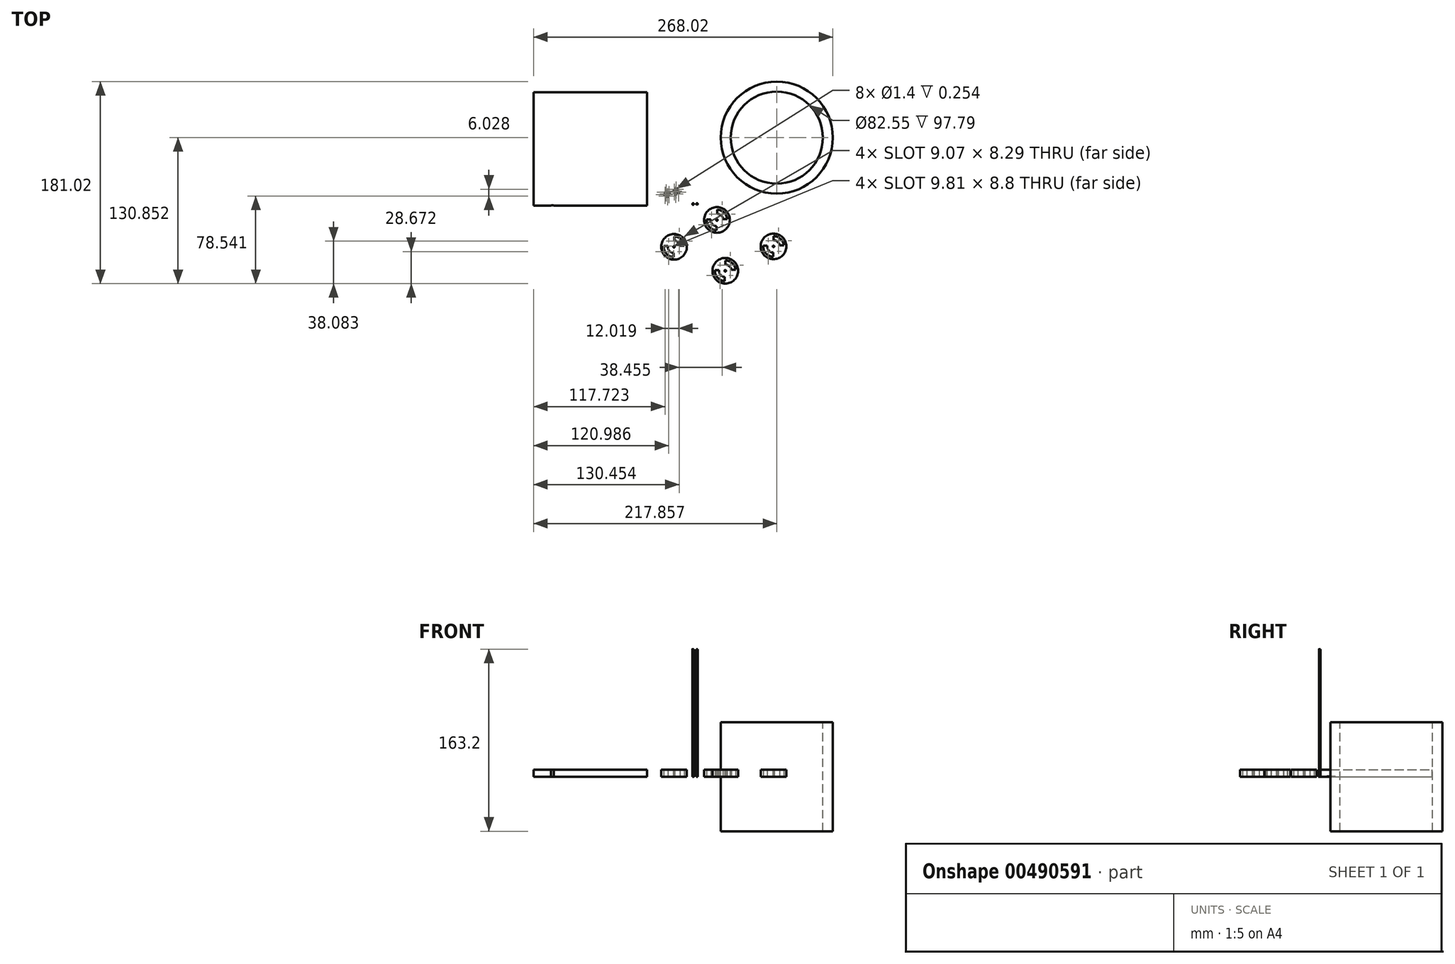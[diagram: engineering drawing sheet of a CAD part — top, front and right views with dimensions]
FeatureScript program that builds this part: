
annotation { "Feature Type Name" : "Feature", "Feature Type Description" : "" }
export const myFeature = defineFeature(function(context is Context, id is Id, definition is map)
    precondition{}
    {
        {
            var Q0;
            Q0=qCreatedBy(makeId("Top.planeOp"),FACE);
            var sketch = newSketch(context, id + "F0", { "sketchPlane" : qUnion([Q0])});
            skPoint(sketch, "E0.middle", {"position": v(-57.24, 51.22) * mm});
            skLineSegment(sketch, "E1.bottom", {"start": v(-104.05, -41.76) * mm, "end": v(-2.45, -41.76) * mm});
            skLineSegment(sketch, "E1.top", {"start": v(-104.05, 59.84) * mm, "end": v(-2.45, 59.84) * mm});
            skLineSegment(sketch, "E1.left", {"start": v(-104.05, -41.76) * mm, "end": v(-104.05, 59.84) * mm});
            skLineSegment(sketch, "E1.right", {"start": v(-2.45, -41.76) * mm, "end": v(-2.45, 59.84) * mm});
            skCircle(sketch, "E2", {"center": v(-87.23, -48.35) * mm, "radius": 6.73 * mm});
            skSolve(sketch);
        }
        {
            var Q0;
            Q0=makeQuery(id+"F0.imprint","IMPRINT",FACE,{"disambiguationData":[TD([[makeQuery(id+"F0.imprint","IMPRINT",EDGE,{"derivedFrom":sQuery(id+"F0.wireOp",EDGE,"set8GWzY-VPnI-Jl6J-Yfnt-XFd2aHyLtcpZ.bottom")}),-1.0]])]});
            var Q1;
            Q1=makeQuery(id+"F0.imprint","IMPRINT",FACE,{"disambiguationData":[TD([[makeQuery(id+"F0.imprint","IMPRINT",EDGE,{"derivedFrom":sQuery(id+"F0.wireOp",EDGE,"E1.bottom")}),1.0]])]});
            extrude(context, id + "F1", {"entities" : qUnion([Q0, Q1]), "depth" : 6.1 * mm, "offsetDistance" : 25.4 * mm});
        }
        {
            var Q0;
            Q0=qCreatedBy(makeId("Top.planeOp"),FACE);
            var sketch = newSketch(context, id + "F2", { "sketchPlane" : qUnion([Q0])});
            skCircle(sketch, "E3", {"center": v(113.8, 19.11) * mm, "radius": 50.17 * mm});
            skCircle(sketch, "E4", {"center": v(113.8, 19.11) * mm, "radius": 41.28 * mm});
            skSolve(sketch);
        }
        {
            var Q0;
            Q0=makeQuery(id+"F2.imprint","IMPRINT",FACE,{"disambiguationData":[TD([[makeQuery(id+"F2.imprint","IMPRINT",EDGE,{"derivedFrom":sQuery(id+"F2.wireOp",EDGE,"E3")}),1.0]])]});
            var Q1;
            Q1=makeQuery(id+"F2.imprint","IMPRINT",FACE,{"disambiguationData":[TD([[makeQuery(id+"F2.imprint","IMPRINT",EDGE,{"derivedFrom":sQuery(id+"F2.wireOp",EDGE,"8FLB0VX2-9ZDr-e1oo-BQHL-Wdt3ujgGbvWg")}),1.0]])]});
            extrude(context, id + "F3", {"entities" : qUnion([Q0, Q1]), "endBound" : BoundingType.SYMMETRIC, "oppositeDirection" : true, "depth" : -97.8 * mm, "offsetDistance" : 25.4 * mm});
        }
        {
            var Q0;
            Q0=qCreatedBy(makeId("Top.planeOp"),FACE);
            var sketch = newSketch(context, id + "F4", { "sketchPlane" : qUnion([Q0])});
            skCircle(sketch, "E5", {"center": v(60.2, -54.7) * mm, "radius": 11.5 * mm});
            skArc(sketch, "E6", {"start": v(59.24, -45.52) * mm, "mid": v(53.78, -48.08) * mm, "end": v(51.05, -53.46) * mm});
            skCircle(sketch, "E7", {"center": v(60.2, -54.7) * mm, "radius": 0.7 * mm});
            skArc(sketch, "E8", {"start": v(60.47, -60.24) * mm, "mid": v(64.31, -58.43) * mm, "end": v(65.74, -54.43) * mm});
            skLineSegment(sketch, "E9", {"start": v(59.24, -45.52) * mm, "end": v(59.24, -49.25) * mm});
            skLineSegment(sketch, "E10", {"start": v(60.32, -45.44) * mm, "end": v(60.32, -49.17) * mm});
            skLineSegment(sketch, "E11", {"start": v(59.8, -60.23) * mm, "end": v(59.8, -63.93) * mm});
            skLineSegment(sketch, "E12", {"start": v(65.67, -53.77) * mm, "end": v(69.4, -53.77) * mm});
            skLineSegment(sketch, "E13", {"start": v(65.74, -54.43) * mm, "end": v(69.44, -54.43) * mm});
            skLineSegment(sketch, "E14", {"start": v(54.8, -53.46) * mm, "end": v(51.05, -53.46) * mm});
            skLineSegment(sketch, "E15", {"start": v(54.7, -54.13) * mm, "end": v(50.99, -54.13) * mm});
            skLineSegment(sketch, "E16", {"start": v(60.47, -60.24) * mm, "end": v(60.47, -63.94) * mm});
            skCircle(sketch, "E17", {"center": v(110.86, -78.39) * mm, "radius": 11.5 * mm});
            skArc(sketch, "E18", {"start": v(109.9, -69.2) * mm, "mid": v(104.43, -71.76) * mm, "end": v(101.7, -77.14) * mm});
            skCircle(sketch, "E19", {"center": v(110.86, -78.39) * mm, "radius": 0.7 * mm});
            skArc(sketch, "E20", {"start": v(105.35, -77.8) * mm, "mid": v(106.6, -81.93) * mm, "end": v(110.44, -83.9) * mm});
            skLineSegment(sketch, "E21", {"start": v(109.9, -69.2) * mm, "end": v(109.9, -72.93) * mm});
            skLineSegment(sketch, "E22", {"start": v(110.97, -69.12) * mm, "end": v(110.97, -72.85) * mm});
            skLineSegment(sketch, "E23", {"start": v(110.44, -83.9) * mm, "end": v(110.44, -87.61) * mm});
            skLineSegment(sketch, "E24", {"start": v(116.32, -77.44) * mm, "end": v(120.05, -77.44) * mm});
            skLineSegment(sketch, "E25", {"start": v(116.39, -78.1) * mm, "end": v(120.1, -78.1) * mm});
            skLineSegment(sketch, "E26", {"start": v(105.46, -77.14) * mm, "end": v(101.7, -77.14) * mm});
            skLineSegment(sketch, "E27", {"start": v(105.35, -77.8) * mm, "end": v(101.64, -77.8) * mm});
            skLineSegment(sketch, "E28", {"start": v(111.13, -83.92) * mm, "end": v(111.13, -87.62) * mm});
            skCircle(sketch, "E29", {"center": v(67.64, -100.24) * mm, "radius": 11.5 * mm});
            skArc(sketch, "E30", {"start": v(66.68, -91.06) * mm, "mid": v(61.21, -93.61) * mm, "end": v(58.5, -99) * mm});
            skCircle(sketch, "E31", {"center": v(67.64, -100.24) * mm, "radius": 0.7 * mm});
            skArc(sketch, "E32", {"start": v(73.1, -99.3) * mm, "mid": v(71.26, -96.04) * mm, "end": v(67.76, -94.7) * mm});
            skLineSegment(sketch, "E33", {"start": v(66.68, -91.06) * mm, "end": v(66.68, -94.79) * mm});
            skLineSegment(sketch, "E34", {"start": v(67.76, -90.97) * mm, "end": v(67.76, -94.7) * mm});
            skLineSegment(sketch, "E35", {"start": v(67.23, -105.76) * mm, "end": v(67.23, -109.47) * mm});
            skLineSegment(sketch, "E36", {"start": v(73.1, -99.3) * mm, "end": v(76.83, -99.3) * mm});
            skLineSegment(sketch, "E37", {"start": v(73.18, -99.96) * mm, "end": v(76.88, -99.96) * mm});
            skLineSegment(sketch, "E38", {"start": v(62.25, -99) * mm, "end": v(58.5, -99) * mm});
            skLineSegment(sketch, "E39", {"start": v(62.14, -99.66) * mm, "end": v(58.43, -99.66) * mm});
            skLineSegment(sketch, "E40", {"start": v(67.91, -105.77) * mm, "end": v(67.91, -109.47) * mm});
            skCircle(sketch, "E41", {"center": v(21.75, -78.75) * mm, "radius": 11.5 * mm});
            skArc(sketch, "E42", {"start": v(20.79, -69.56) * mm, "mid": v(15.32, -72.12) * mm, "end": v(12.6, -77.5) * mm});
            skCircle(sketch, "E43", {"center": v(21.75, -78.75) * mm, "radius": 0.7 * mm});
            skArc(sketch, "E44", {"start": v(16.24, -78.16) * mm, "mid": v(17.5, -82.3) * mm, "end": v(21.34, -84.27) * mm});
            skLineSegment(sketch, "E45", {"start": v(20.79, -69.56) * mm, "end": v(20.79, -73.3) * mm});
            skLineSegment(sketch, "E46", {"start": v(21.87, -69.48) * mm, "end": v(21.87, -73.2) * mm});
            skLineSegment(sketch, "E47", {"start": v(21.34, -84.27) * mm, "end": v(21.34, -87.97) * mm});
            skLineSegment(sketch, "E48", {"start": v(27.21, -77.8) * mm, "end": v(30.94, -77.8) * mm});
            skLineSegment(sketch, "E49", {"start": v(27.28, -78.47) * mm, "end": v(30.98, -78.47) * mm});
            skLineSegment(sketch, "E50", {"start": v(16.36, -77.5) * mm, "end": v(12.6, -77.5) * mm});
            skLineSegment(sketch, "E51", {"start": v(16.24, -78.16) * mm, "end": v(12.53, -78.16) * mm});
            skLineSegment(sketch, "E52", {"start": v(22.02, -84.28) * mm, "end": v(22.02, -87.98) * mm});
            skArc(sketch, "E53.trimOffspring", {"start": v(69.4, -53.77) * mm, "mid": v(66.44, -47.9) * mm, "end": v(60.32, -45.47) * mm});
            skArc(sketch, "E54.trimOffspring", {"start": v(50.99, -54.13) * mm, "mid": v(53.33, -60.88) * mm, "end": v(59.8, -63.93) * mm});
            skArc(sketch, "E55.trimOffspring", {"start": v(60.47, -63.94) * mm, "mid": v(66.93, -61.04) * mm, "end": v(69.44, -54.43) * mm});
            skArc(sketch, "E56.trimOffspring", {"start": v(54.7, -54.13) * mm, "mid": v(55.95, -58.26) * mm, "end": v(59.8, -60.23) * mm});
            skArc(sketch, "E57.trimOffspring", {"start": v(59.24, -49.25) * mm, "mid": v(56.4, -50.7) * mm, "end": v(54.8, -53.46) * mm});
            skArc(sketch, "E58.trimOffspring", {"start": v(65.67, -53.77) * mm, "mid": v(63.82, -50.5) * mm, "end": v(60.32, -49.17) * mm});
            skArc(sketch, "E59.trimOffspring", {"start": v(120.05, -77.44) * mm, "mid": v(117.1, -71.57) * mm, "end": v(110.97, -69.15) * mm});
            skArc(sketch, "E60.trimOffspring", {"start": v(111.13, -87.62) * mm, "mid": v(117.58, -84.72) * mm, "end": v(120.1, -78.1) * mm});
            skArc(sketch, "E61.trimOffspring", {"start": v(101.64, -77.8) * mm, "mid": v(103.98, -84.55) * mm, "end": v(110.44, -87.61) * mm});
            skArc(sketch, "E62.trimOffspring", {"start": v(109.9, -72.93) * mm, "mid": v(107.04, -74.37) * mm, "end": v(105.46, -77.14) * mm});
            skArc(sketch, "E63.trimOffspring", {"start": v(116.32, -77.44) * mm, "mid": v(114.47, -74.19) * mm, "end": v(110.97, -72.85) * mm});
            skArc(sketch, "E64.trimOffspring", {"start": v(111.13, -83.92) * mm, "mid": v(114.96, -82.1) * mm, "end": v(116.39, -78.1) * mm});
            skArc(sketch, "E65.trimOffspring", {"start": v(76.83, -99.3) * mm, "mid": v(73.88, -93.42) * mm, "end": v(67.76, -91) * mm});
            skArc(sketch, "E66.trimOffspring", {"start": v(58.43, -99.66) * mm, "mid": v(60.77, -106.4) * mm, "end": v(67.23, -109.47) * mm});
            skArc(sketch, "E67.trimOffspring", {"start": v(67.91, -109.47) * mm, "mid": v(74.37, -106.58) * mm, "end": v(76.88, -99.96) * mm});
            skArc(sketch, "E68.trimOffspring", {"start": v(66.68, -94.79) * mm, "mid": v(63.83, -96.23) * mm, "end": v(62.25, -99) * mm});
            skArc(sketch, "E69.trimOffspring", {"start": v(62.14, -99.66) * mm, "mid": v(63.4, -103.79) * mm, "end": v(67.23, -105.76) * mm});
            skArc(sketch, "E70.trimOffspring", {"start": v(67.91, -105.77) * mm, "mid": v(71.75, -103.96) * mm, "end": v(73.18, -99.96) * mm});
            skArc(sketch, "E71.trimOffspring", {"start": v(12.53, -78.16) * mm, "mid": v(21.6, -87.98) * mm, "end": v(30.98, -78.47) * mm});
            skArc(sketch, "E72.trimOffspring", {"start": v(22.02, -84.28) * mm, "mid": v(25.86, -82.46) * mm, "end": v(27.28, -78.47) * mm});
            skArc(sketch, "E73.trimOffspring", {"start": v(27.21, -77.8) * mm, "mid": v(21.9, -73.2) * mm, "end": v(16.36, -77.5) * mm});
            skArc(sketch, "E74.trimOffspring", {"start": v(30.94, -77.8) * mm, "mid": v(27.98, -71.93) * mm, "end": v(21.87, -69.5) * mm});
            skSolve(sketch);
        }
        {
            var Q0;
            Q0=makeQuery(id+"F4.imprint","IMPRINT",FACE,{"disambiguationData":[TD([[makeQuery(id+"F4.imprint","IMPRINT",EDGE,{"derivedFrom":sQuery(id+"F4.wireOp",EDGE,"E5")}),1.0]])]});
            var Q1;
            {var subQ0=sQuery(id+"F4.wireOp",EDGE,"E14");Q1=makeQuery(id+"F4.imprint","IMPRINT",FACE,{"disambiguationData":[TD([[makeQuery(id+"F4.imprint","IMPRINT",EDGE,{"derivedFrom":subQ0}),1.0]])]});}
            var Q2;
            {var subQ0=sQuery(id+"F4.wireOp",EDGE,"E11");Q2=makeQuery(id+"F4.imprint","IMPRINT",FACE,{"disambiguationData":[TD([[makeQuery(id+"F4.imprint","IMPRINT",EDGE,{"derivedFrom":subQ0}),1.0]])]});}
            var Q3;
            {var subQ0=sQuery(id+"F4.wireOp",EDGE,"E13");Q3=makeQuery(id+"F4.imprint","IMPRINT",FACE,{"disambiguationData":[TD([[makeQuery(id+"F4.imprint","IMPRINT",EDGE,{"derivedFrom":subQ0}),-1.0]])]});}
            var Q4;
            {var subQ0=sQuery(id+"F4.wireOp",EDGE,"E9");Q4=makeQuery(id+"F4.imprint","IMPRINT",FACE,{"disambiguationData":[TD([[makeQuery(id+"F4.imprint","IMPRINT",EDGE,{"derivedFrom":subQ0}),-1.0]])]});}
            var Q5;
            {var subQ0=sQuery(id+"F4.wireOp",EDGE,"E9");Q5=makeQuery(id+"F4.imprint","IMPRINT",FACE,{"disambiguationData":[TD([[makeQuery(id+"F4.imprint","IMPRINT",EDGE,{"derivedFrom":subQ0}),1.0]])]});}
            var Q6;
            Q6=makeQuery(id+"F4.imprint","IMPRINT",FACE,{"disambiguationData":[TD([[makeQuery(id+"F4.imprint","IMPRINT",EDGE,{"derivedFrom":sQuery(id+"F4.wireOp",EDGE,"E7")}),-1.0]])]});
            var Q7;
            {var subQ0=sQuery(id+"F4.wireOp",EDGE,"E21");Q7=makeQuery(id+"F4.imprint","IMPRINT",FACE,{"disambiguationData":[TD([[makeQuery(id+"F4.imprint","IMPRINT",EDGE,{"derivedFrom":subQ0}),1.0]])]});}
            var Q8;
            Q8=makeQuery(id+"F4.imprint","IMPRINT",FACE,{"disambiguationData":[TD([[makeQuery(id+"F4.imprint","IMPRINT",EDGE,{"derivedFrom":sQuery(id+"F4.wireOp",EDGE,"E19")}),-1.0]])]});
            var Q9;
            {var subQ0=sQuery(id+"F4.wireOp",EDGE,"E26");Q9=makeQuery(id+"F4.imprint","IMPRINT",FACE,{"disambiguationData":[TD([[makeQuery(id+"F4.imprint","IMPRINT",EDGE,{"derivedFrom":subQ0}),1.0]])]});}
            var Q10;
            {var subQ0=sQuery(id+"F4.wireOp",EDGE,"E25");Q10=makeQuery(id+"F4.imprint","IMPRINT",FACE,{"disambiguationData":[TD([[makeQuery(id+"F4.imprint","IMPRINT",EDGE,{"derivedFrom":subQ0}),-1.0]])]});}
            var Q11;
            {var subQ0=sQuery(id+"F4.wireOp",EDGE,"E23");Q11=makeQuery(id+"F4.imprint","IMPRINT",FACE,{"disambiguationData":[TD([[makeQuery(id+"F4.imprint","IMPRINT",EDGE,{"derivedFrom":subQ0}),1.0]])]});}
            var Q12;
            {var subQ0=sQuery(id+"F4.wireOp",EDGE,"E21");Q12=makeQuery(id+"F4.imprint","IMPRINT",FACE,{"disambiguationData":[TD([[makeQuery(id+"F4.imprint","IMPRINT",EDGE,{"derivedFrom":subQ0}),-1.0]])]});}
            var Q13;
            {var subQ0=sQuery(id+"F4.wireOp",EDGE,"E24");Q13=makeQuery(id+"F4.imprint","IMPRINT",FACE,{"disambiguationData":[TD([[makeQuery(id+"F4.imprint","IMPRINT",EDGE,{"derivedFrom":subQ0}),-1.0]])]});}
            var Q14;
            Q14=makeQuery(id+"F4.imprint","IMPRINT",FACE,{"disambiguationData":[TD([[makeQuery(id+"F4.imprint","IMPRINT",EDGE,{"derivedFrom":sQuery(id+"F4.wireOp",EDGE,"E17")}),1.0]])]});
            var Q15;
            Q15=makeQuery(id+"F4.imprint","IMPRINT",FACE,{"disambiguationData":[TD([[makeQuery(id+"F4.imprint","IMPRINT",EDGE,{"derivedFrom":sQuery(id+"F4.wireOp",EDGE,"E41")}),1.0]])]});
            var Q16;
            {var subQ0=sQuery(id+"F4.wireOp",EDGE,"E50");Q16=makeQuery(id+"F4.imprint","IMPRINT",FACE,{"disambiguationData":[TD([[makeQuery(id+"F4.imprint","IMPRINT",EDGE,{"derivedFrom":subQ0}),1.0]])]});}
            var Q17;
            {var subQ0=sQuery(id+"F4.wireOp",EDGE,"E45");Q17=makeQuery(id+"F4.imprint","IMPRINT",FACE,{"disambiguationData":[TD([[makeQuery(id+"F4.imprint","IMPRINT",EDGE,{"derivedFrom":subQ0}),-1.0]])]});}
            var Q18;
            {var subQ0=sQuery(id+"F4.wireOp",EDGE,"E47");Q18=makeQuery(id+"F4.imprint","IMPRINT",FACE,{"disambiguationData":[TD([[makeQuery(id+"F4.imprint","IMPRINT",EDGE,{"derivedFrom":subQ0}),1.0]])]});}
            var Q19;
            {var subQ0=sQuery(id+"F4.wireOp",EDGE,"E49");Q19=makeQuery(id+"F4.imprint","IMPRINT",FACE,{"disambiguationData":[TD([[makeQuery(id+"F4.imprint","IMPRINT",EDGE,{"derivedFrom":subQ0}),-1.0]])]});}
            var Q20;
            {var subQ0=sQuery(id+"F4.wireOp",EDGE,"E45");Q20=makeQuery(id+"F4.imprint","IMPRINT",FACE,{"disambiguationData":[TD([[makeQuery(id+"F4.imprint","IMPRINT",EDGE,{"derivedFrom":subQ0}),1.0]])]});}
            var Q21;
            {var subQ0=sQuery(id+"F4.wireOp",EDGE,"E48");Q21=makeQuery(id+"F4.imprint","IMPRINT",FACE,{"disambiguationData":[TD([[makeQuery(id+"F4.imprint","IMPRINT",EDGE,{"derivedFrom":subQ0}),-1.0]])]});}
            var Q22;
            Q22=makeQuery(id+"F4.imprint","IMPRINT",FACE,{"disambiguationData":[TD([[makeQuery(id+"F4.imprint","IMPRINT",EDGE,{"derivedFrom":sQuery(id+"F4.wireOp",EDGE,"E43")}),-1.0]])]});
            var Q23;
            {var subQ0=sQuery(id+"F4.wireOp",EDGE,"E33");Q23=makeQuery(id+"F4.imprint","IMPRINT",FACE,{"disambiguationData":[TD([[makeQuery(id+"F4.imprint","IMPRINT",EDGE,{"derivedFrom":subQ0}),1.0]])]});}
            var Q24;
            {var subQ0=sQuery(id+"F4.wireOp",EDGE,"E38");Q24=makeQuery(id+"F4.imprint","IMPRINT",FACE,{"disambiguationData":[TD([[makeQuery(id+"F4.imprint","IMPRINT",EDGE,{"derivedFrom":subQ0}),1.0]])]});}
            var Q25;
            {var subQ0=sQuery(id+"F4.wireOp",EDGE,"E36");Q25=makeQuery(id+"F4.imprint","IMPRINT",FACE,{"disambiguationData":[TD([[makeQuery(id+"F4.imprint","IMPRINT",EDGE,{"derivedFrom":subQ0}),-1.0]])]});}
            var Q26;
            Q26=makeQuery(id+"F4.imprint","IMPRINT",FACE,{"disambiguationData":[TD([[makeQuery(id+"F4.imprint","IMPRINT",EDGE,{"derivedFrom":sQuery(id+"F4.wireOp",EDGE,"E31")}),-1.0]])]});
            var Q27;
            {var subQ0=sQuery(id+"F4.wireOp",EDGE,"E33");Q27=makeQuery(id+"F4.imprint","IMPRINT",FACE,{"disambiguationData":[TD([[makeQuery(id+"F4.imprint","IMPRINT",EDGE,{"derivedFrom":subQ0}),-1.0]])]});}
            var Q28;
            {var subQ0=sQuery(id+"F4.wireOp",EDGE,"E35");Q28=makeQuery(id+"F4.imprint","IMPRINT",FACE,{"disambiguationData":[TD([[makeQuery(id+"F4.imprint","IMPRINT",EDGE,{"derivedFrom":subQ0}),1.0]])]});}
            var Q29;
            Q29=makeQuery(id+"F4.imprint","IMPRINT",FACE,{"disambiguationData":[TD([[makeQuery(id+"F4.imprint","IMPRINT",EDGE,{"derivedFrom":sQuery(id+"F4.wireOp",EDGE,"E29")}),1.0]])]});
            var Q30;
            {var subQ0=sQuery(id+"F4.wireOp",EDGE,"E37");Q30=makeQuery(id+"F4.imprint","IMPRINT",FACE,{"disambiguationData":[TD([[makeQuery(id+"F4.imprint","IMPRINT",EDGE,{"derivedFrom":subQ0}),-1.0]])]});}
            var Q31;
            {var subQ0=sQuery(id+"F4.wireOp",EDGE,"E37");Q31=makeQuery(id+"F4.imprint","IMPRINT",FACE,{"disambiguationData":[TD([[makeQuery(id+"F4.imprint","IMPRINT",EDGE,{"derivedFrom":subQ0}),-1.0]])]});}
            extrude(context, id + "F5", {"entities" : qUnion([Q0, Q1, Q2, Q3, Q4, Q5, Q6, Q7, Q8, Q9, Q10, Q11, Q12, Q13, Q14, Q15, Q16, Q17, Q18, Q19, Q20, Q21, Q22, Q23, Q24, Q25, Q26, Q27, Q28, Q29, Q30, Q31]), "depth" : 6.1 * mm, "offsetDistance" : 25.4 * mm});
        }
        {
            var Q0;
            Q0=qCreatedBy(makeId("Top.planeOp"),FACE);
            var sketch = newSketch(context, id + "F6", { "sketchPlane" : qUnion([Q0])});
            skCircle(sketch, "E75", {"center": v(38.82, -40.4) * mm, "radius": 0.69 * mm});
            skCircle(sketch, "E76", {"center": v(42.33, -40.4) * mm, "radius": 0.69 * mm});
            skSolve(sketch);
        }
        {
            var Q0;
            Q0=makeQuery(id+"F6.imprint","IMPRINT",FACE,{"disambiguationData":[TD([[makeQuery(id+"F6.imprint","IMPRINT",EDGE,{"derivedFrom":sQuery(id+"F6.wireOp",EDGE,"E75")}),1.0]])]});
            var Q1;
            Q1=makeQuery(id+"F6.imprint","IMPRINT",FACE,{"disambiguationData":[TD([[makeQuery(id+"F6.imprint","IMPRINT",EDGE,{"derivedFrom":sQuery(id+"F6.wireOp",EDGE,"E76")}),1.0]])]});
            extrude(context, id + "F7", {"entities" : qUnion([Q0, Q1]), "depth" : 114.3 * mm, "offsetDistance" : 25.4 * mm});
        }
        {
            var Q0;
            Q0=qCreatedBy(makeId("Top.planeOp"),FACE);
            var sketch = newSketch(context, id + "F8", { "sketchPlane" : qUnion([Q0])});
            skCircle(sketch, "E77", {"center": v(14.73, -29.75) * mm, "radius": 0.83 * mm});
            skCircle(sketch, "E78", {"center": v(14.73, -29.75) * mm, "radius": 0.7 * mm});
            skCircle(sketch, "E79", {"center": v(17.27, -31.28) * mm, "radius": 0.83 * mm});
            skCircle(sketch, "E80", {"center": v(17.27, -31.28) * mm, "radius": 0.7 * mm});
            skCircle(sketch, "E81", {"center": v(16.09, -33.2) * mm, "radius": 0.83 * mm});
            skCircle(sketch, "E82", {"center": v(16.09, -33.2) * mm, "radius": 0.7 * mm});
            skCircle(sketch, "E83", {"center": v(13.67, -31.94) * mm, "radius": 0.83 * mm});
            skCircle(sketch, "E84", {"center": v(13.67, -31.94) * mm, "radius": 0.7 * mm});
            skCircle(sketch, "E85", {"center": v(22, -28.9) * mm, "radius": 0.83 * mm});
            skCircle(sketch, "E86", {"center": v(22, -28.9) * mm, "radius": 0.7 * mm});
            skCircle(sketch, "E87", {"center": v(23.51, -27.17) * mm, "radius": 0.83 * mm});
            skCircle(sketch, "E88", {"center": v(23.51, -27.17) * mm, "radius": 0.7 * mm});
            skCircle(sketch, "E89", {"center": v(23.22, -31.27) * mm, "radius": 0.83 * mm});
            skCircle(sketch, "E90", {"center": v(23.22, -31.27) * mm, "radius": 0.7 * mm});
            skCircle(sketch, "E91", {"center": v(25.7, -29.8) * mm, "radius": 0.83 * mm});
            skCircle(sketch, "E92", {"center": v(25.7, -29.8) * mm, "radius": 0.7 * mm});
            skSolve(sketch);
        }
        {
            var Q0;
            Q0 = qSketchRegion(id + "F8", true);
            extrude(context, id + "F9", {"entities" : qUnion([Q0]), "depth" : 0.25 * mm, "offsetDistance" : 25.4 * mm});
        }
        {
            var Q0;
            Q0=qCreatedBy(makeId("Top.planeOp"),FACE);
            var sketch = newSketch(context, id + "F10", { "sketchPlane" : qUnion([Q0])});
            skCircle(sketch, "E93", {"center": v(12.23, 18.26) * mm, "radius": 0.67 * mm});
            skCircle(sketch, "E94", {"center": v(14.72, 17.64) * mm, "radius": 0.67 * mm});
            skCircle(sketch, "E95", {"center": v(16.18, 20.09) * mm, "radius": 0.67 * mm});
            skCircle(sketch, "E96", {"center": v(12.9, 21) * mm, "radius": 0.67 * mm});
            skSolve(sketch);
        }
        {
            var Q0;
            Q0 = qConstructionFilter(qBodyType(qCreatedBy(id + "F10" ,EDGE), BodyType.WIRE), ConstructionObject.NO);
            extrude(context, id + "F11", {"bodyType" : ToolBodyType.SURFACE, "surfaceEntities" : qUnion([Q0]), "depth" : 50.8 * mm, "offsetDistance" : 25.4 * mm});
        }
    });
